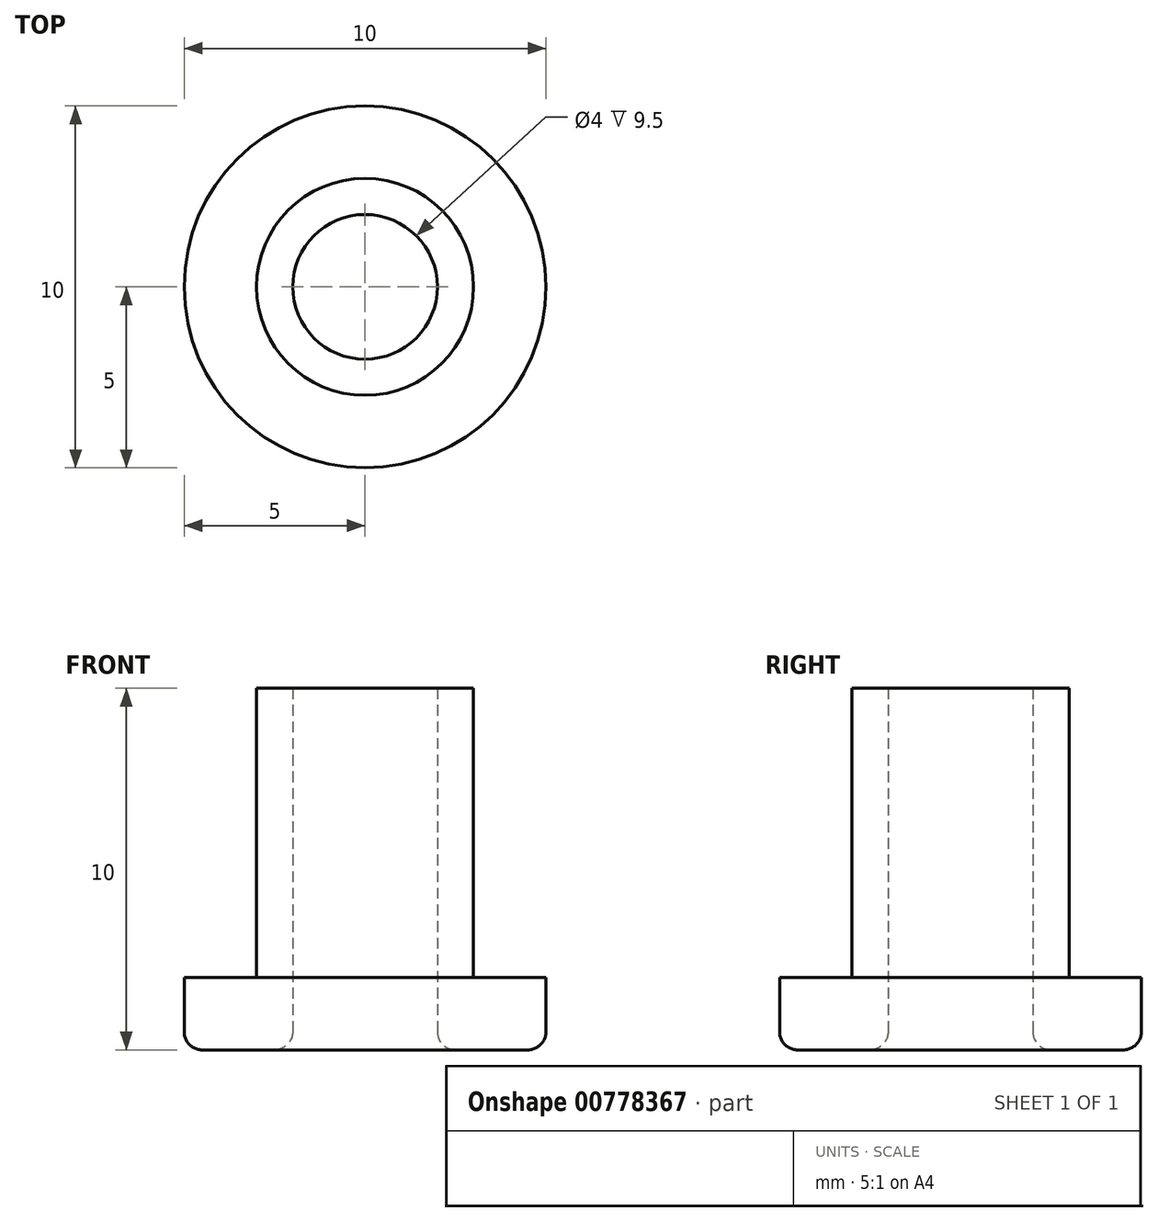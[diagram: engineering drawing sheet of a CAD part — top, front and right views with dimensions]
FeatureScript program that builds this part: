
annotation { "Feature Type Name" : "Feature", "Feature Type Description" : "" }
export const myFeature = defineFeature(function(context is Context, id is Id, definition is map)
    precondition{}
    {
        {
            var Q0;
            Q0=qCreatedBy(makeId("Top.planeOp"),FACE);
            var sketch = newSketch(context, id + "F0", { "sketchPlane" : qUnion([Q0])});
            skCircle(sketch, "E0", {"center": v(0, 0) * mm, "radius": 2 * mm});
            skCircle(sketch, "E1", {"center": v(0, 0) * mm, "radius": 3 * mm});
            skCircle(sketch, "E2", {"center": v(0, 0) * mm, "radius": 5 * mm});
            skSolve(sketch);
        }
        {
            var Q0;
            Q0=makeQuery(id+"F0.imprint","IMPRINT",FACE,{"disambiguationData":[TD([[makeQuery(id+"F0.imprint","IMPRINT",EDGE,{"derivedFrom":sQuery(id+"F0.wireOp",EDGE,"E0")}),-1.0]])]});
            extrude(context, id + "F1", {"entities" : qUnion([Q0]), "depth" : 10 * mm, "offsetDistance" : 25 * mm});
        }
        {
            var Q0;
            Q0=makeQuery(id+"F0.imprint","IMPRINT",FACE,{"disambiguationData":[TD([[makeQuery(id+"F0.imprint","IMPRINT",EDGE,{"derivedFrom":sQuery(id+"F0.wireOp",EDGE,"E1")}),-1.0]])]});
            extrude(context, id + "F2", {"entities" : qUnion([Q0]), "operationType" : NewBodyOperationType.ADD, "depth" : 2 * mm, "offsetDistance" : 25 * mm});
        }
        {
            var Q0;
            Q0=makeQuery(id+"F2.opExtrude","CAP_EDGE",EDGE,{"disambiguationData":[OSD([sQuery(id+"F0.wireOp",EDGE,"E2")])],"isStart":true});
            var Q1;
            Q1=makeQuery(id+"F1.opExtrude","CAP_EDGE",EDGE,{"disambiguationData":[OSD([sQuery(id+"F0.wireOp",EDGE,"E0")])],"isStart":true});
            fillet(context, id + "F3", {"entities" : qUnion([Q0, Q1]), "radius" : 0.5 * mm, "tangentPropagation" : true, "allowEdgeOverflow" : false});
        }
    });
